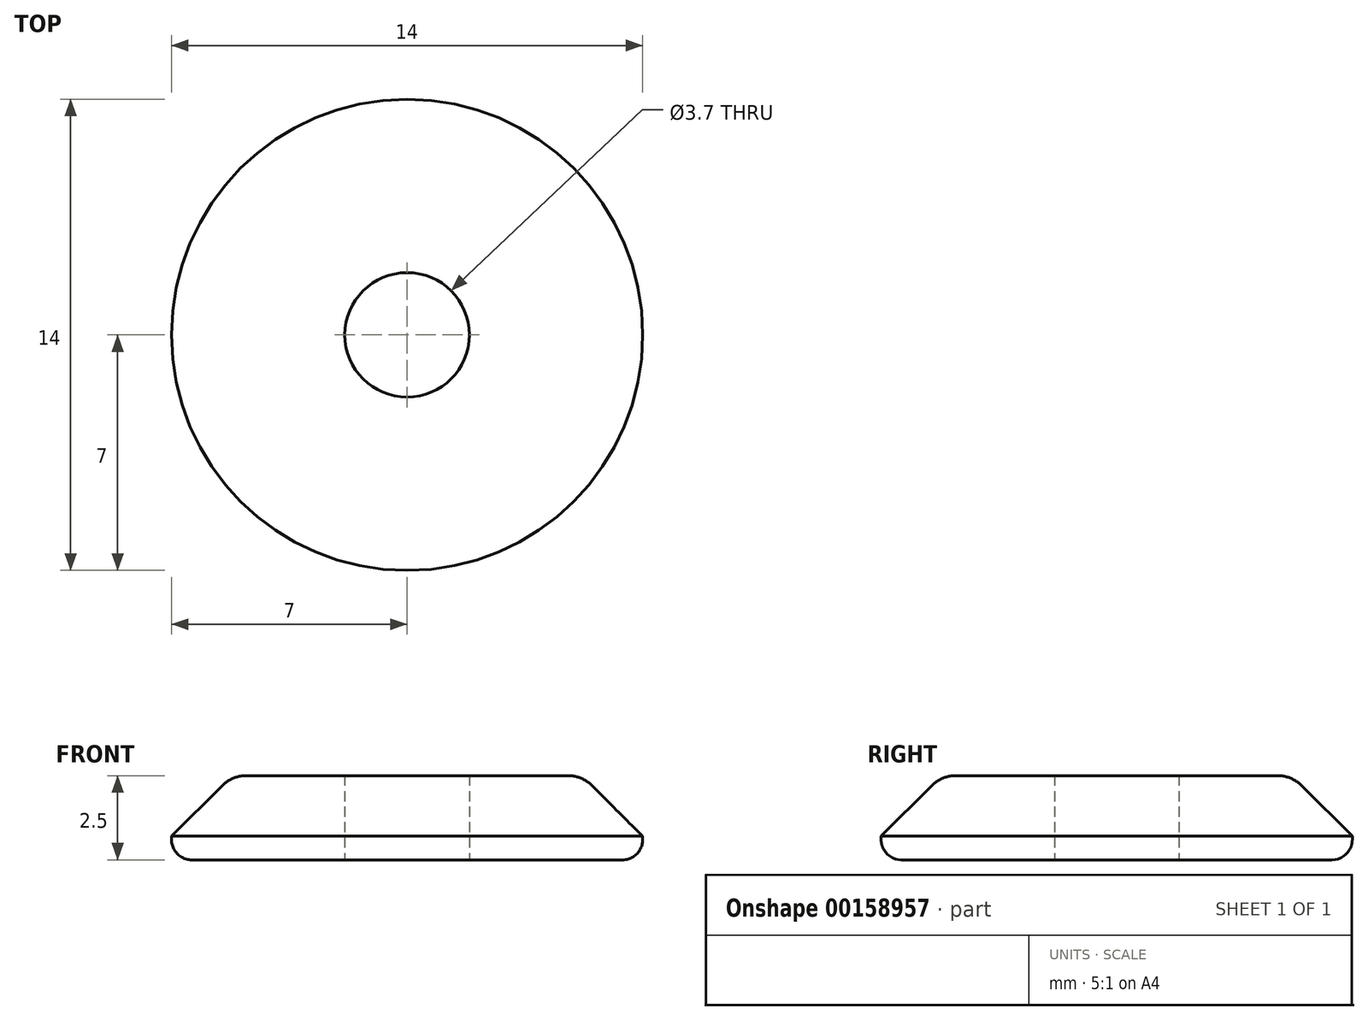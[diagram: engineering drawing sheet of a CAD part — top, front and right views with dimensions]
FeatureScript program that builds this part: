
annotation { "Feature Type Name" : "Feature", "Feature Type Description" : "" }
export const myFeature = defineFeature(function(context is Context, id is Id, definition is map)
    precondition{}
    {
        {
            var Q0;
            Q0=qCreatedBy(makeId("Top.planeOp"),FACE);
            var sketch = newSketch(context, id + "F0", { "sketchPlane" : qUnion([Q0])});
            skCircle(sketch, "E0", {"center": v(0, 0) * mm, "radius": 7 * mm});
            skCircle(sketch, "E1", {"center": v(0, 0) * mm, "radius": 1.85 * mm});
            skSolve(sketch);
        }
        {
            var Q0;
            Q0 = qSketchRegion(id + "F0", true);
            extrude(context, id + "F1", {"entities" : qUnion([Q0]), "depth" : 2.5 * mm});
        }
        {
            var Q0;
            Q0=makeQuery(id+"F1.opExtrude","CAP_EDGE",EDGE,{"disambiguationData":[OSD([sQuery(id+"F0.wireOp",EDGE,"E0")])],"isStart":false});
            chamfer(context, id + "F2", {"entities" : qUnion([Q0]), "width" : 1.8 * mm, "tangentPropagation" : true});
        }
        {
            var Q0;
            Q0=makeQuery(id+"F1.opExtrude","CAP_EDGE",EDGE,{"disambiguationData":[OSD([sQuery(id+"F0.wireOp",EDGE,"E0")])],"isStart":true});
            fillet(context, id + "F3", {"entities" : qUnion([Q0]), "radius" : 0.6 * mm, "tangentPropagation" : true, "allowEdgeOverflow" : false});
        }
        {
            var Q0;
            {var subQ0=sQuery(id+"F0.wireOp",EDGE,"E0");Q0=makeQuery(id+"F2.opChamfer","BLEND_EDGE",EDGE,{"blendedFrom":[makeQuery(id+"F1.opExtrude","CAP_EDGE",EDGE,{"disambiguationData":[OSD([subQ0])],"isStart":false}),makeQuery(id+"F1.opExtrude","CAP_FACE",FACE,{"disambiguationData":[OSD([subQ0,sQuery(id+"F0.wireOp",EDGE,"E1")])],"isStart":false})],"blendedInto":[makeQuery(id+"F1.opExtrude","CAP_FACE",FACE,{"disambiguationData":[OSD([subQ0,sQuery(id+"F0.wireOp",EDGE,"E1")])],"isStart":false})]});}
            fillet(context, id + "F4", {"entities" : qUnion([Q0]), "radius" : 1 * mm, "tangentPropagation" : true, "allowEdgeOverflow" : false});
        }
    });
